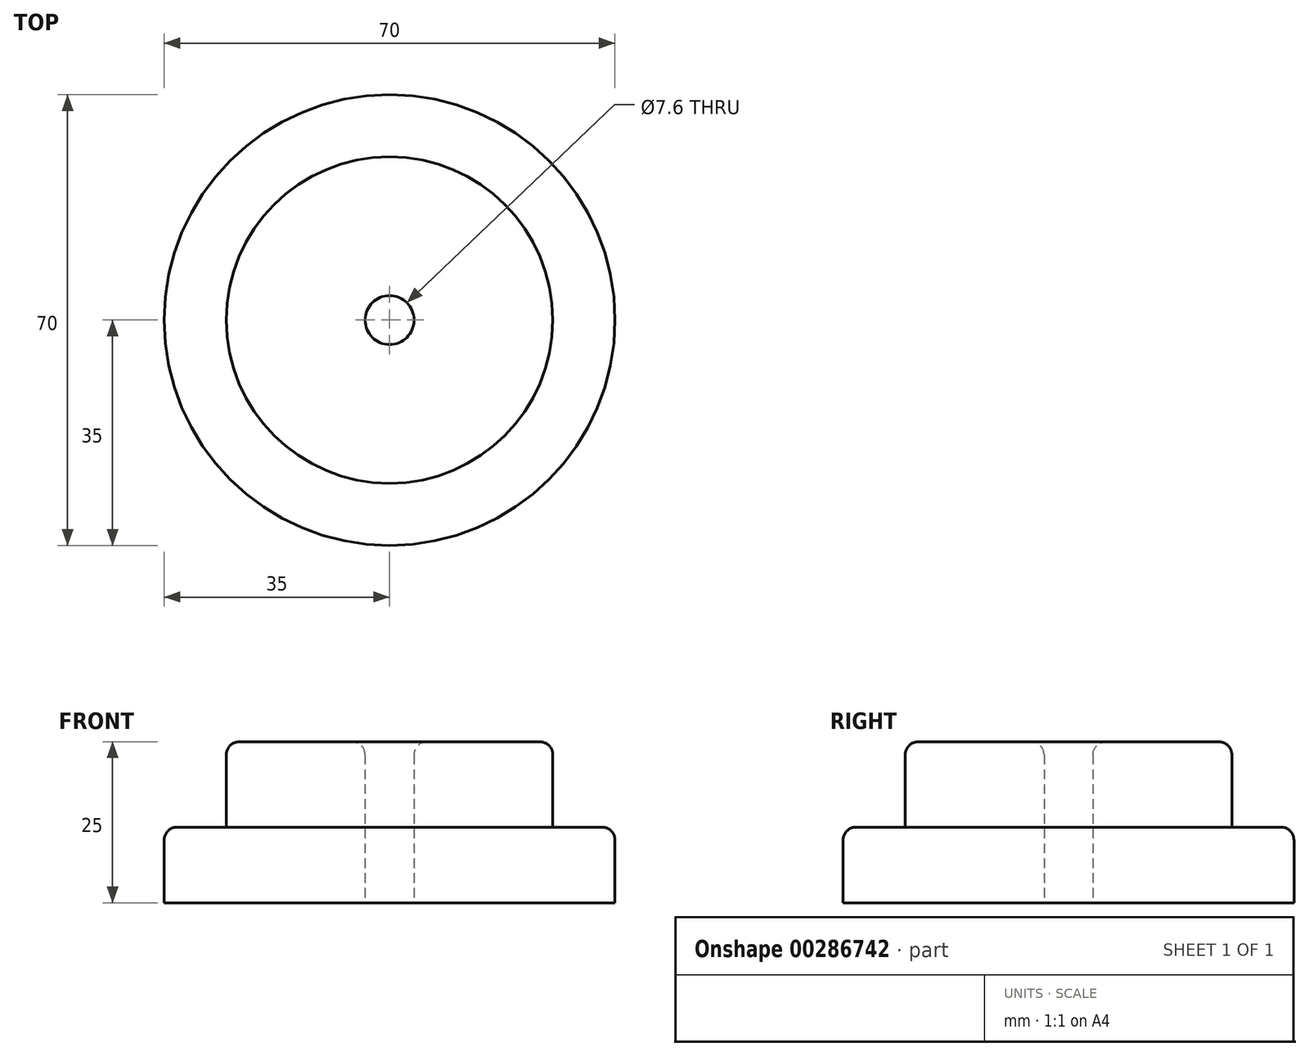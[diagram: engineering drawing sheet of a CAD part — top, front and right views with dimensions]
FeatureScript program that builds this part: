
annotation { "Feature Type Name" : "Feature", "Feature Type Description" : "" }
export const myFeature = defineFeature(function(context is Context, id is Id, definition is map)
    precondition{}
    {
        {
            var Q0;
            Q0=qCreatedBy(makeId("Top.planeOp"),FACE);
            var sketch = newSketch(context, id + "F0", { "sketchPlane" : qUnion([Q0])});
            skCircle(sketch, "E0", {"center": v(0, 0) * mm, "radius": 25.35 * mm});
            skCircle(sketch, "E1", {"center": v(0, 0) * mm, "radius": 35 * mm});
            skCircle(sketch, "E2", {"center": v(0, 0) * mm, "radius": 3.8 * mm});
            skSolve(sketch);
        }
        {
            var Q0;
            Q0=makeQuery(id+"F0.imprint","IMPRINT",FACE,{"disambiguationData":[TD([[makeQuery(id+"F0.imprint","IMPRINT",EDGE,{"derivedFrom":sQuery(id+"F0.wireOp",EDGE,"E0")}),-1.0]])]});
            extrude(context, id + "F1", {"entities" : qUnion([Q0]), "depth" : 11.75 * mm});
        }
        {
            var Q0;
            Q0=makeQuery(id+"F0.imprint","IMPRINT",FACE,{"disambiguationData":[TD([[makeQuery(id+"F0.imprint","IMPRINT",EDGE,{"derivedFrom":sQuery(id+"F0.wireOp",EDGE,"E0")}),1.0]])]});
            extrude(context, id + "F2", {"entities" : qUnion([Q0]), "operationType" : NewBodyOperationType.ADD, "depth" : 25 * mm});
        }
        {
            var Q0;
            Q0=makeQuery(id+"F1.opExtrude","CAP_EDGE",EDGE,{"disambiguationData":[OSD([sQuery(id+"F0.wireOp",EDGE,"E1")])],"isStart":false});
            var Q1;
            Q1=makeQuery(id+"F2.opExtrude","CAP_EDGE",EDGE,{"disambiguationData":[OSD([sQuery(id+"F0.wireOp",EDGE,"E0")])],"isStart":false});
            var Q2;
            Q2=makeQuery(id+"F2.opExtrude","CAP_EDGE",EDGE,{"disambiguationData":[OSD([sQuery(id+"F0.wireOp",EDGE,"E2")])],"isStart":false});
            fillet(context, id + "F3", {"entities" : qUnion([Q0, Q1, Q2]), "radius" : 2 * mm, "tangentPropagation" : true, "allowEdgeOverflow" : false});
        }
    });
